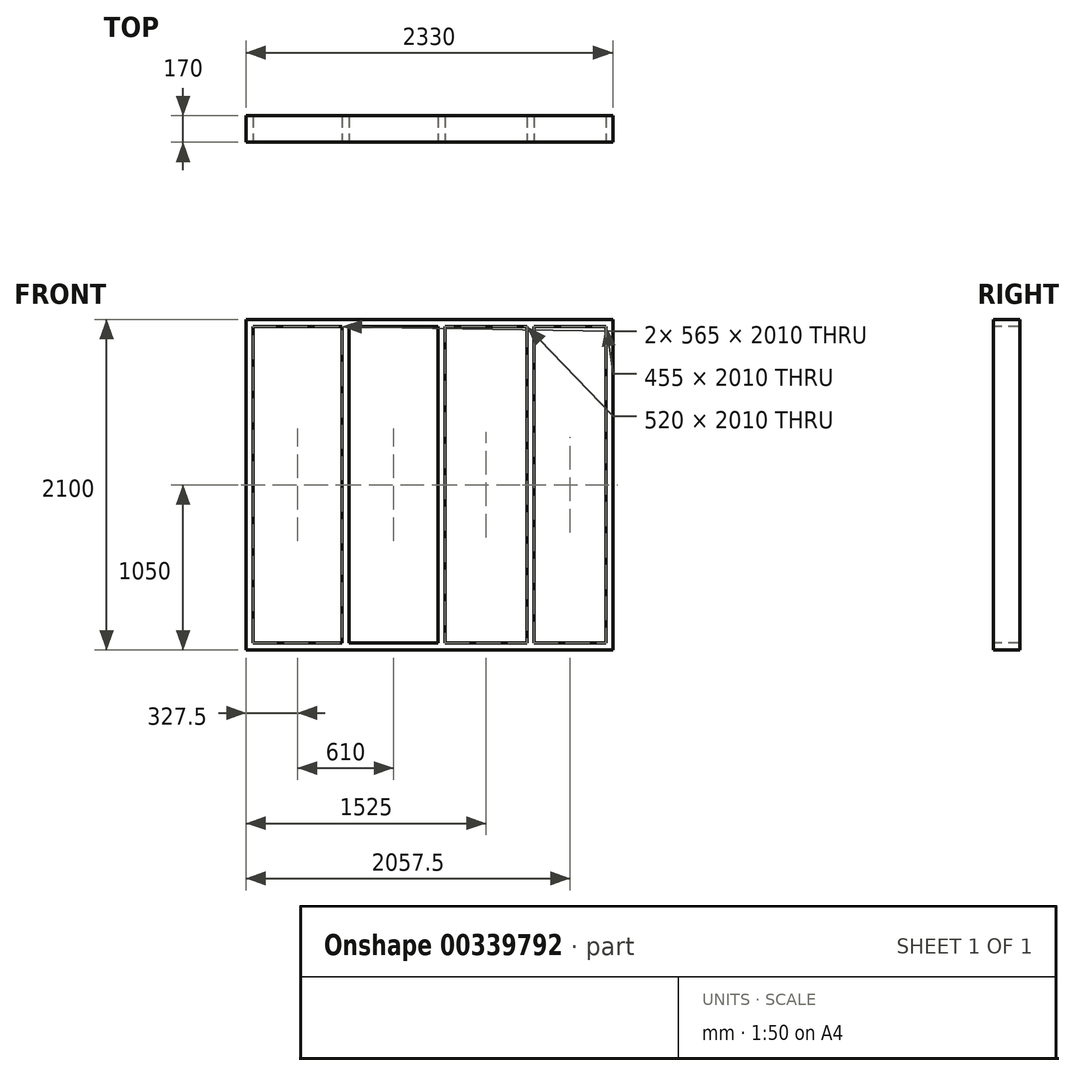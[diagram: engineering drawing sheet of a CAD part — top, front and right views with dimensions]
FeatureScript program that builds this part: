
annotation { "Feature Type Name" : "Feature", "Feature Type Description" : "" }
export const myFeature = defineFeature(function(context is Context, id is Id, definition is map)
    precondition{}
    {
        {
            var Q0;
            Q0=qCreatedBy(makeId("Front.planeOp"),FACE);
            var sketch = newSketch(context, id + "F0", { "sketchPlane" : qUnion([Q0])});
            skLineSegment(sketch, "E0.bottom", {"start": v(0, 0) * mm, "end": v(2330, 0) * mm});
            skLineSegment(sketch, "E0.top", {"start": v(0, 2100) * mm, "end": v(2330, 2100) * mm});
            skLineSegment(sketch, "E0.left", {"start": v(0, 0) * mm, "end": v(0, 2100) * mm});
            skLineSegment(sketch, "E0.right", {"start": v(2330, 0) * mm, "end": v(2330, 2100) * mm});
            skLineSegment(sketch, "E1.0", {"start": v(45, 45) * mm, "end": v(45, 2055) * mm});
            skLineSegment(sketch, "E2.0", {"start": v(610, 45) * mm, "end": v(610, 2055) * mm});
            skLineSegment(sketch, "E3.0", {"start": v(655, 45) * mm, "end": v(655, 2055) * mm});
            skLineSegment(sketch, "E4.0", {"start": v(1265, 45) * mm, "end": v(1265, 2055) * mm});
            skLineSegment(sketch, "E5.0", {"start": v(1830, 45) * mm, "end": v(1830, 2055) * mm});
            skLineSegment(sketch, "E6.0", {"start": v(1785, 45) * mm, "end": v(1785, 2055) * mm});
            skLineSegment(sketch, "E7.0", {"start": v(2285, 45) * mm, "end": v(2285, 2055) * mm});
            skLineSegment(sketch, "E8.0", {"start": v(45, 2055) * mm, "end": v(610, 2055) * mm});
            skLineSegment(sketch, "E9.0", {"start": v(45, 45) * mm, "end": v(610, 45) * mm});
            skLineSegment(sketch, "E10.trimOffspring", {"start": v(655, 2055) * mm, "end": v(1220, 2055) * mm});
            skLineSegment(sketch, "E11.trimOffspring", {"start": v(1265, 2055) * mm, "end": v(1785, 2055) * mm});
            skLineSegment(sketch, "E12.trimOffspring", {"start": v(1265, 45) * mm, "end": v(1785, 45) * mm});
            skLineSegment(sketch, "E13.trimOffspring", {"start": v(655, 45) * mm, "end": v(1220, 45) * mm});
            skLineSegment(sketch, "E14.trimOffspring", {"start": v(1830, 45) * mm, "end": v(2285, 45) * mm});
            skLineSegment(sketch, "E15.trimOffspring", {"start": v(1830, 2055) * mm, "end": v(2285, 2055) * mm});
            skLineSegment(sketch, "E16", {"start": v(1220, 2055) * mm, "end": v(1220, 45) * mm});
            skSolve(sketch);
        }
        {
            var Q0;
            {var subQ8=sQuery(id+"F0.wireOp",EDGE,"E0.top");Q0=makeQuery(id+"F0.imprint","IMPRINT",FACE,{"disambiguationData":[TD([[makeQuery(id+"F0.imprint","IMPRINT",EDGE,{"derivedFrom":subQ8}),-1.0]])]});}
            extrude(context, id + "F1", {"entities" : qUnion([Q0]), "oppositeDirection" : true, "depth" : 170 * mm});
        }
    });
